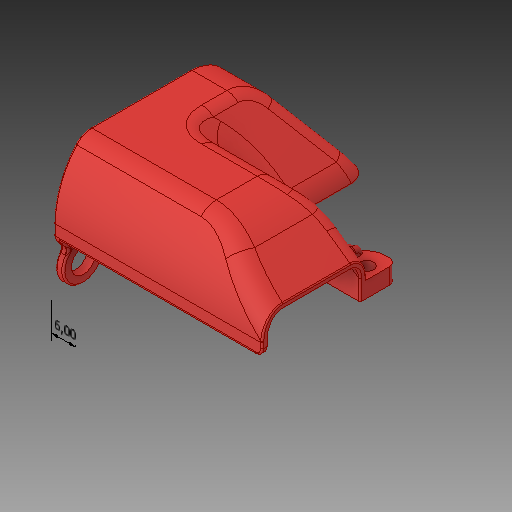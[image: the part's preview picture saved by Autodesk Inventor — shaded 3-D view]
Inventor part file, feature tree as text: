
AUTODESK INVENTOR PART (.ipt)
format: ipt  version: 2019.4 (Build 234330000, 330)  size: 1,345,024 bytes
history: native  units: in
note: dims shown in document units (in); Inventor stores cm internally (conversion verified against a paired STEP export)
features: other x7, fillet x7, extrude x4, sketch x4, plane x2, loft x2, projected_geometry x2
ambient origin geometry x8: Origin, YZ Plane, XZ Plane, XY Plane, X Axis, Y Axis, Z Axis, Center Point
bodies: Solid1 (feature_tree)
feature tree (28):
  other  "Annotations"
  plane  "Work Plane1"
  extrude  "Extrusion1"  Depth=0.315in TaperAngle=0.0deg
  plane  "Work Plane2"
  extrude  "Extrusion2"  Depth=0.0197in
  fillet  "Fillet1"  Radius=0.2362in
  extrude  "Extrusion3"  Depth=0.3937in
  fillet  "Fillet2"  Radius=0.3937in
  fillet  "Fillet3"  Radius=0.8661in
  fillet  "Fillet4"  Radius=0.3937in
  fillet  "Fillet5"  Radius=0.3937in
  fillet  "Fillet6"  Radius=0.2362in
  extrude  "Extrusion4"  Depth=0.1969in
  loft  "Loft1"
  loft  "Loft3"
  fillet  "Fillet8"  Radius=0.0157in
  sketch  "Sketch3"  dims[d4=-0.0394in d5=0.315in d6=0.0in]
  sketch  "Sketch4"  dims[d7=0.2756in d8=0.0in d15=0.0197in d16=0.2362in]
  sketch  "Sketch5"  dims[d17=0.2362in d18=0.3937in d19=0.3937in d20=0.8661in d22=0.3937in d23=0.3937in d24=0.2362in]
  other  "Edges1"
  other  "Edges3"
  sketch  "Sketch11"  dims[d25=0.2362in d26=0.1969in d27=0.1575in d28=0.3937in d29=0.0in d30=0.0157in d31=0.0157in d32=0.315in d33=0.315in d34=0.0591in d37=0.3937in d38=0.0in d39=0.0in d40=90.0deg d44=90.0deg d45=0.0in d46=90.0deg d58=0.0in d59=90.0deg d60=0.0in d61=90.0deg d62=0.0118in d10=0.1674in d11=0.0787in d12=-0.4302in d13=-0.17in d14=0.2362in d9=0.2838in]
  other  "Edges5"
  other  "[a]_connector_cover"
  projected_geometry  "Project Cut Edges1"
  projected_geometry  "Project Cut Edges2"
  other  "Linear Dimension 1"
  other  "Linear Dimension 2"
